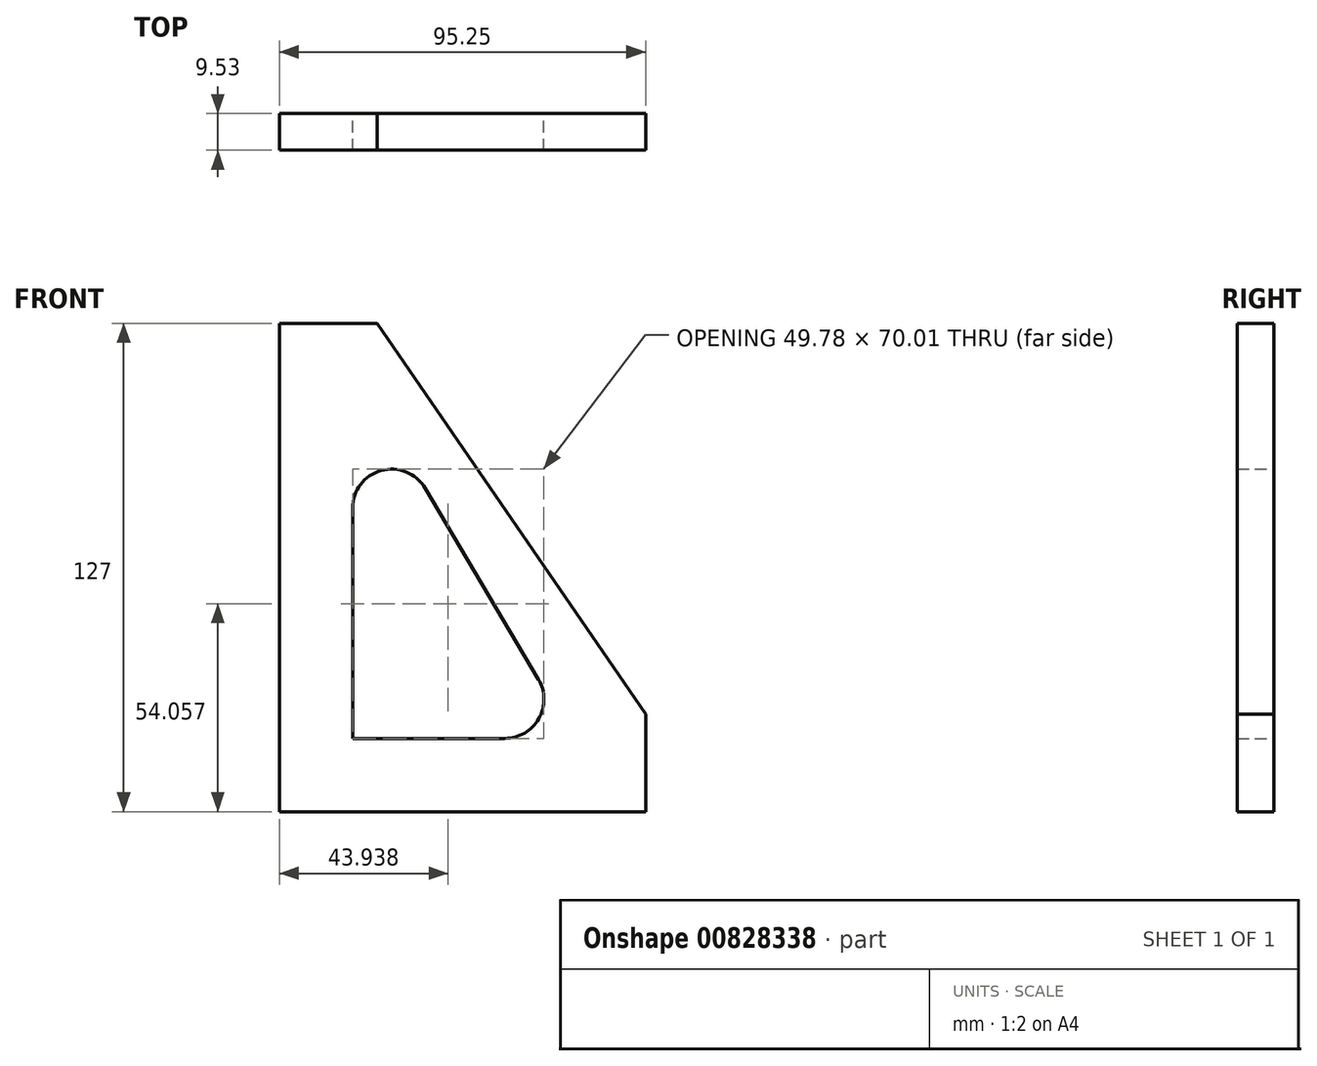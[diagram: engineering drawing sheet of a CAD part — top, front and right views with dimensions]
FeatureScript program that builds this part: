
annotation { "Feature Type Name" : "Feature", "Feature Type Description" : "" }
export const myFeature = defineFeature(function(context is Context, id is Id, definition is map)
    precondition{}
    {
        {
            var Q0;
            Q0=qCreatedBy(makeId("Front.planeOp"),FACE);
            var sketch = newSketch(context, id + "F0", { "sketchPlane" : qUnion([Q0])});
            skLineSegment(sketch, "E0", {"start": v(0, 0) * mm, "end": v(0, 127) * mm});
            skLineSegment(sketch, "E1", {"start": v(0, 127) * mm, "end": v(25.4, 127) * mm});
            skLineSegment(sketch, "E2", {"start": v(0, 0) * mm, "end": v(95.25, 0) * mm});
            skLineSegment(sketch, "E3", {"start": v(95.25, 0) * mm, "end": v(95.25, 25.4) * mm});
            skLineSegment(sketch, "E4", {"start": v(95.25, 25.4) * mm, "end": v(25.4, 127) * mm});
            skLineSegment(sketch, "E5", {"start": v(54.11, 51.61) * mm, "end": v(69.8, 62.4) * mm, "construction": true});
            skLineSegment(sketch, "E6", {"start": v(0, 54.65) * mm, "end": v(19.05, 54.65) * mm});
            skLineSegment(sketch, "E7", {"start": v(40.43, 0) * mm, "end": v(40.43, 19.05) * mm, "construction": true});
            skLineSegment(sketch, "E8", {"start": v(40.43, 19.05) * mm, "end": v(0, 19.05) * mm, "construction": true});
            skLineSegment(sketch, "E9", {"start": v(29.21, 19.05) * mm, "end": v(95.25, 19.05) * mm, "construction": true});
            skLineSegment(sketch, "E10", {"start": v(54.11, 51.61) * mm, "end": v(76.5, 19.05) * mm, "construction": true});
            skLineSegment(sketch, "E11", {"start": v(76.5, 19.05) * mm, "end": v(22.44, 97.68) * mm, "construction": true});
            skLineSegment(sketch, "E12", {"start": v(19.05, 54.65) * mm, "end": v(19.05, 29.21) * mm, "construction": true});
            skLineSegment(sketch, "E13", {"start": v(19.05, 19.05) * mm, "end": v(19.05, 116) * mm, "construction": true});
            skLineSegment(sketch, "E14", {"start": v(19.05, 78.92) * mm, "end": v(19.05, 19.05) * mm});
            skLineSegment(sketch, "E15", {"start": v(67.4, 34.39) * mm, "end": v(37.95, 84.1) * mm});
            skPoint(sketch, "E16.visualSharp", {"position": v(19.05, 116) * mm});
            skArc(sketch, "E16.filletArc", {"start": v(37.95, 84.1) * mm, "mid": v(26.52, 88.72) * mm, "end": v(19.05, 78.92) * mm});
            skLineSegment(sketch, "E17", {"start": v(58.67, 19.05) * mm, "end": v(19.05, 19.05) * mm});
            skPoint(sketch, "E18.visualSharp", {"position": v(76.5, 19.05) * mm});
            skArc(sketch, "E18.filletArc", {"start": v(58.67, 19.05) * mm, "mid": v(67.5, 24.18) * mm, "end": v(67.4, 34.39) * mm});
            skArc(sketch, "E19.filletArc", {"start": v(19.05, 29.21) * mm, "mid": v(22.03, 22.03) * mm, "end": v(29.21, 19.05) * mm, "construction": true});
            skSolve(sketch);
        }
        {
            var Q0;
            Q0 = qSketchRegion(id + "F0", true);
            extrude(context, id + "F1", {"entities" : qUnion([Q0]), "depth" : 9.52 * mm, "offsetDistance" : 25.4 * mm});
        }
    });
